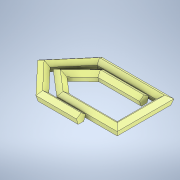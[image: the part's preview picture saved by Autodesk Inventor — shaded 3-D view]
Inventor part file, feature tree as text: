
AUTODESK INVENTOR PART (.ipt)
format: ipt  version: 2021 (Build 250183000, 183)  size: 150,016 bytes
history: native  units: in
note: dims shown in document units (in); Inventor stores cm internally (conversion verified against a paired STEP export)
features: sketch x2, plane x1, sweep x1
ambient origin geometry x8: Origin, YZ Plane, XZ Plane, XY Plane, X Axis, Y Axis, Z Axis, Center Point
bodies: Solid1 (feature_tree)
feature tree (4):
  sketch  "Sketch1"  dims[d0=0.0in d1=0.0in d2=0.0817in]
  plane  "Work Plane1"
  sweep  "Sweep1"
  sketch  "Sketch2"
